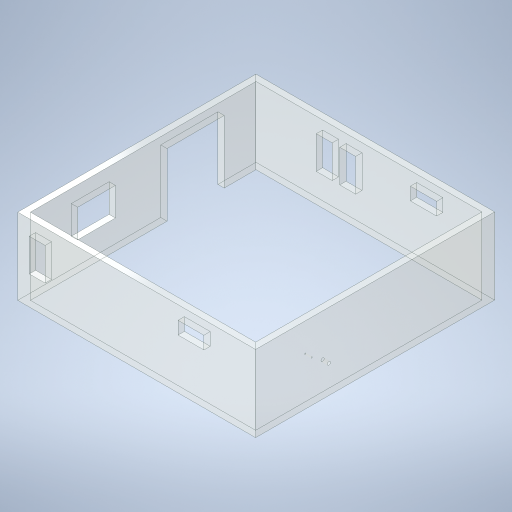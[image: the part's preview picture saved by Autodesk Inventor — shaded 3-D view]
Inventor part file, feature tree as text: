
AUTODESK INVENTOR PART (.ipt)
format: ipt  version: 2024.1 (Build 281209000, 209)  size: 355,840 bytes
history: native  units: in
note: dims shown in document units (in); Inventor stores cm internally (conversion verified against a paired STEP export)
features: sketch x10, extrude x8, hole x2
ambient origin geometry x8: Origin, YZ Plane, XZ Plane, XY Plane, X Axis, Y Axis, Z Axis, Center Point
bodies: Solid1 (feature_tree)
feature tree (20):
  extrude  "Extrusion1"  Depth=0.5in
  hole  "Hole1"  [1 undecoded]
  hole  "Hole2"  [1 undecoded]
  extrude  "Extrusion3"  Depth=96.0in
  extrude  "Extrusion4"  Depth=0.75in
  extrude  "Extrusion5"  Depth=0.75in TaperAngle=0.0deg
  extrude  "Extrusion6"  Depth=79.0in
  extrude  "Extrusion7"  Depth=72.0in TaperAngle=0.0deg
  extrude  "Extrusion8"  Depth=47.5in
  extrude  "Extrusion16"  Depth=35.5in
  sketch  "Sketch1"  dims[d1=283.0in d3=0.5in]
  sketch  "Sketch4"  dims[d4=284.0in d5=284.0in]
  sketch  "Sketch5"  dims[d6=8.0in d8=284.0in]
  sketch  "Sketch6"  dims[d9=96.0in d10=0.0in d27=52.375in]
  sketch  "Sketch7"  dims[d29=1.5in d30=0.75in d31=0.375in d32=0.25in d33=0.5635in d34=1.0in d35=0.8108in d36=35.0in]
  sketch  "Sketch8"  dims[d37=200.0in]
  sketch  "Sketch9"  dims[d38=4.0in d39=0.75in d40=0.375in d41=0.25in d42=0.5635in d43=1.0in d44=0.8108in d49=1.0in d50=0.0in]
  sketch  "Sketch10"  dims[d51=40.0in d52=79.0in]
  sketch  "Sketch11"  dims[d53=72.0in d54=1.0in d55=0.0in]
  sketch  "Sketch20"  dims[d56=107.0in d57=47.5in d58=35.5in d59=36.0in d60=1.0in d61=0.0in d63=41.0in d64=20.0in d65=36.0in d66=178.744in d67=1.0in d68=0.0in d69=36.0in d70=41.0in d71=20.0in d72=75.756in d73=1.0in d74=0.0in d75=6.494in d76=41.0in d79=20.0in d80=36.0in d81=1.0in d82=0.0in d119=57.0in d121=16.0in d129=16.0in d132=1.0in d133=0.0in d134=32.5in d135=63.0in d136=33.0in d137=63.0in d138=57.0in d139=62.25in d20=0.5in d21=0.0344in d22=0.5in d23=0.0344in d100=0.5in d101=0.0344in d102=0.5in d103=0.0344in d140=1.0in d141=1.0in d142=1.0in d143=0.15in d144=0.25in d145=0.375in d146=0.5635in d147=0.75in d148=0.8108in d149=0.0625in d150=0.75in d151=0.375in]
note: 2 required parameter values undecoded (feature->parameter linkage not recoverable at this tier; creation-order binding heuristic only, values carry confidence <= 0.55)
